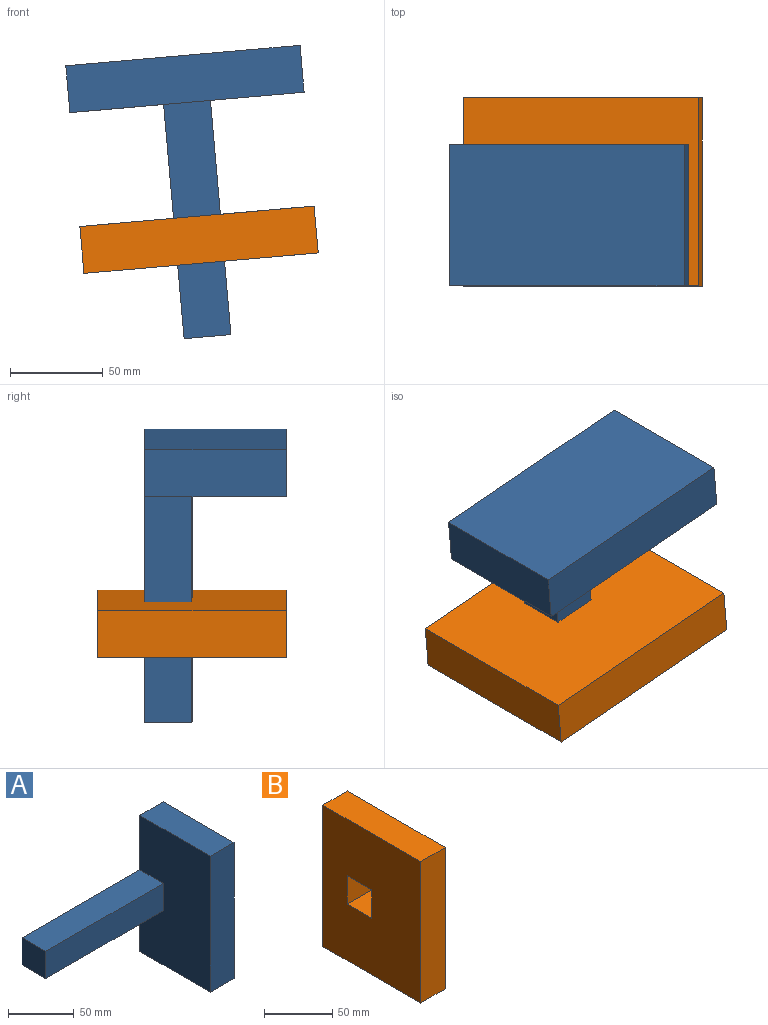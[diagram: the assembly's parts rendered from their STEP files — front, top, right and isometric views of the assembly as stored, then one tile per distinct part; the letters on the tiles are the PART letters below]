
ASSEMBLY  parts=2 mates=1
PART A: 10 faces, bbox 152.4x76.2x127 mm
  f0: plane 127x76.2mm, normal (-1,0,0), area 9032.2mm2, adj f1,f3,f4,f5,f6,f8,f9
  f1: plane 76.2x25.4mm, normal (0,0,-1), area 1935.5mm2, adj f0,f2,f4,f5
  f2: plane 127x76.2mm, normal (1,0,0), area 9677.4mm2, adj f1,f3,f4,f5
  f3: plane 76.2x25.4mm, normal (0,0,1), area 1935.5mm2, adj f0,f2,f4,f5
  f4: plane 127x25.4mm, normal (0,-1,0), area 3225.8mm2, adj f0,f1,f2,f3
  f5: plane 152.4x127mm, normal (0,1,0), area 6451.6mm2, adj f0,f1,f2,f3,f6,f7,f8
  f6: plane 127x25.4mm, normal (0,0,1), area 3225.8mm2, adj f0,f5,f7,f9
  f7: plane 25.4x25.4mm, normal (-1,0,0), area 645.2mm2, adj f5,f6,f8,f9
  f8: plane 127x25.4mm, normal (0,0,-1), area 3225.8mm2, adj f0,f5,f7,f9
  f9: plane 127x25.4mm, normal (0,-1,0), area 3225.8mm2, adj f0,f6,f7,f8
PART B: 10 faces, bbox 25.4x101.6x127 mm
  f0: plane 127x101.6mm, normal (-1,0,0), area 12258mm2, adj f2,f3,f4,f5,f6,f7,f8,f9
  f1: plane 127x101.6mm, normal (1,0,0), area 12258mm2, adj f2,f3,f4,f5,f6,f7,f8,f9
  f2: plane 101.6x25.4mm, normal (0,0,1), area 2580.6mm2, adj f0,f1,f4,f5
  f3: plane 101.6x25.4mm, normal (0,0,-1), area 2580.6mm2, adj f0,f1,f4,f5
  f4: plane 127x25.4mm, normal (0,-1,0), area 3225.8mm2, adj f0,f1,f2,f3
  f5: plane 127x25.4mm, normal (0,1,0), area 3225.8mm2, adj f0,f1,f2,f3
  f6: plane 25.4x25.4mm, normal (0,-1,0), area 645.2mm2, adj f0,f1,f7,f9
  f7: plane 25.4x25.4mm, normal (0,0,-1), area 645.2mm2, adj f0,f1,f6,f8
  f8: plane 25.4x25.4mm, normal (0,1,0), area 645.2mm2, adj f0,f1,f7,f9
  f9: plane 25.4x25.4mm, normal (0,0,1), area 645.2mm2, adj f0,f1,f6,f8
PLACE A rot(axis=(0,-1,0),95deg) t=(-117.78,67.97,31.5)mm
PLACE B rot(axis=(0,-1,0),95deg) t=(-62.12,67.97,25.4)mm
MATE slider B.f1 <-> A.f7  axis (-0.09,0,1) through (-106.45,55.27,33.04)mm
